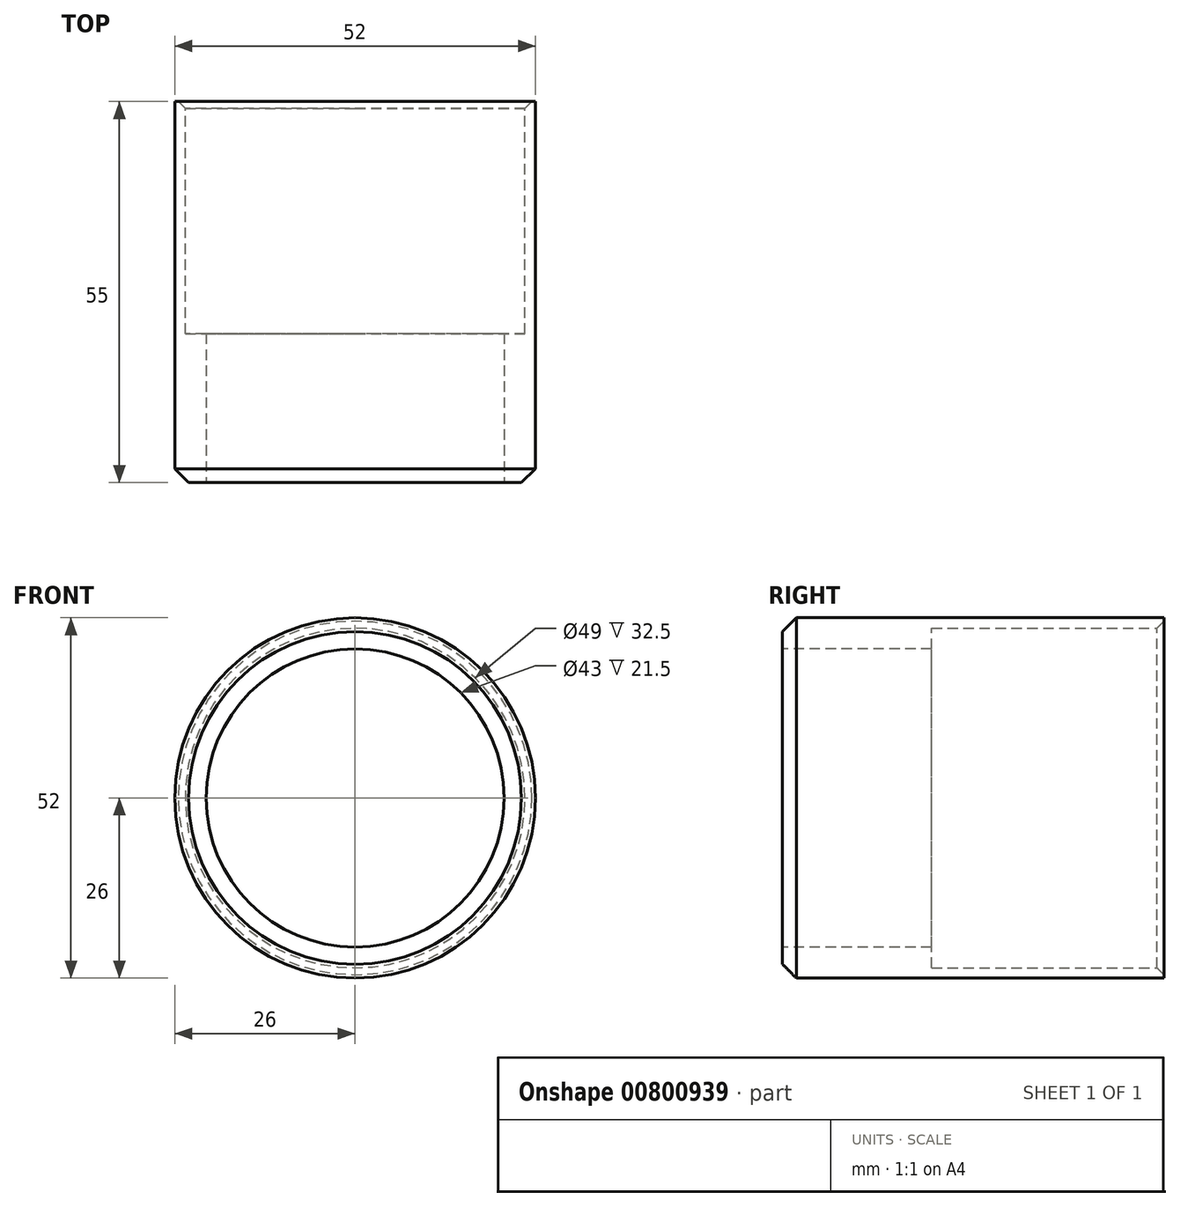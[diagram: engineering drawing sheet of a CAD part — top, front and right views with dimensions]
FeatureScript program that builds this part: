
annotation { "Feature Type Name" : "Feature", "Feature Type Description" : "" }
export const myFeature = defineFeature(function(context is Context, id is Id, definition is map)
    precondition{}
    {
        {
            var Q0;
            Q0=qCreatedBy(makeId("Front.planeOp"),FACE);
            var sketch = newSketch(context, id + "F0", { "sketchPlane" : qUnion([Q0])});
            skCircle(sketch, "E0", {"center": v(0, 0) * mm, "radius": 24.5 * mm});
            skCircle(sketch, "E1", {"center": v(0, 0) * mm, "radius": 26 * mm});
            skSolve(sketch);
        }
        {
            var Q0;
            Q0 = qSketchRegion(id + "F0", true);
            extrude(context, id + "F1", {"entities" : qUnion([Q0]), "depth" : 55 * mm, "offsetDistance" : 25 * mm});
        }
        {
            var Q0;
            Q0=makeQuery(id+"F1.opExtrude","CAP_FACE",FACE,{"disambiguationData":[OSD([sQuery(id+"F0.wireOp",EDGE,"E0"),sQuery(id+"F0.wireOp",EDGE,"E1")])],"isStart":false});
            var sketch = newSketch(context, id + "F2", { "sketchPlane" : qUnion([Q0])});
            skCircle(sketch, "E2", {"center": v(0, 0) * mm, "radius": 21.5 * mm});
            skCircle(sketch, "E3.0", {"center": v(0, 0) * mm, "radius": 24.5 * mm});
            skSolve(sketch);
        }
        {
            var Q0;
            Q0 = qSketchRegion(id + "F2", true);
            extrude(context, id + "F3", {"entities" : qUnion([Q0]), "operationType" : NewBodyOperationType.ADD, "oppositeDirection" : true, "depth" : 21.5 * mm, "offsetDistance" : 25 * mm});
        }
        {
            var Q0;
            Q0=makeQuery(id+"F1.opExtrude","CAP_EDGE",EDGE,{"disambiguationData":[OSD([sQuery(id+"F0.wireOp",EDGE,"E1")])],"isStart":false});
            chamfer(context, id + "F4", {"entities" : qUnion([Q0]), "width" : 2 * mm, "tangentPropagation" : true});
        }
        {
            var Q0;
            Q0=makeQuery(id+"F1.opExtrude","CAP_EDGE",EDGE,{"disambiguationData":[OSD([sQuery(id+"F0.wireOp",EDGE,"E0")])],"isStart":true});
            chamfer(context, id + "F5", {"entities" : qUnion([Q0]), "width" : 1 * mm, "tangentPropagation" : true});
        }
    });
